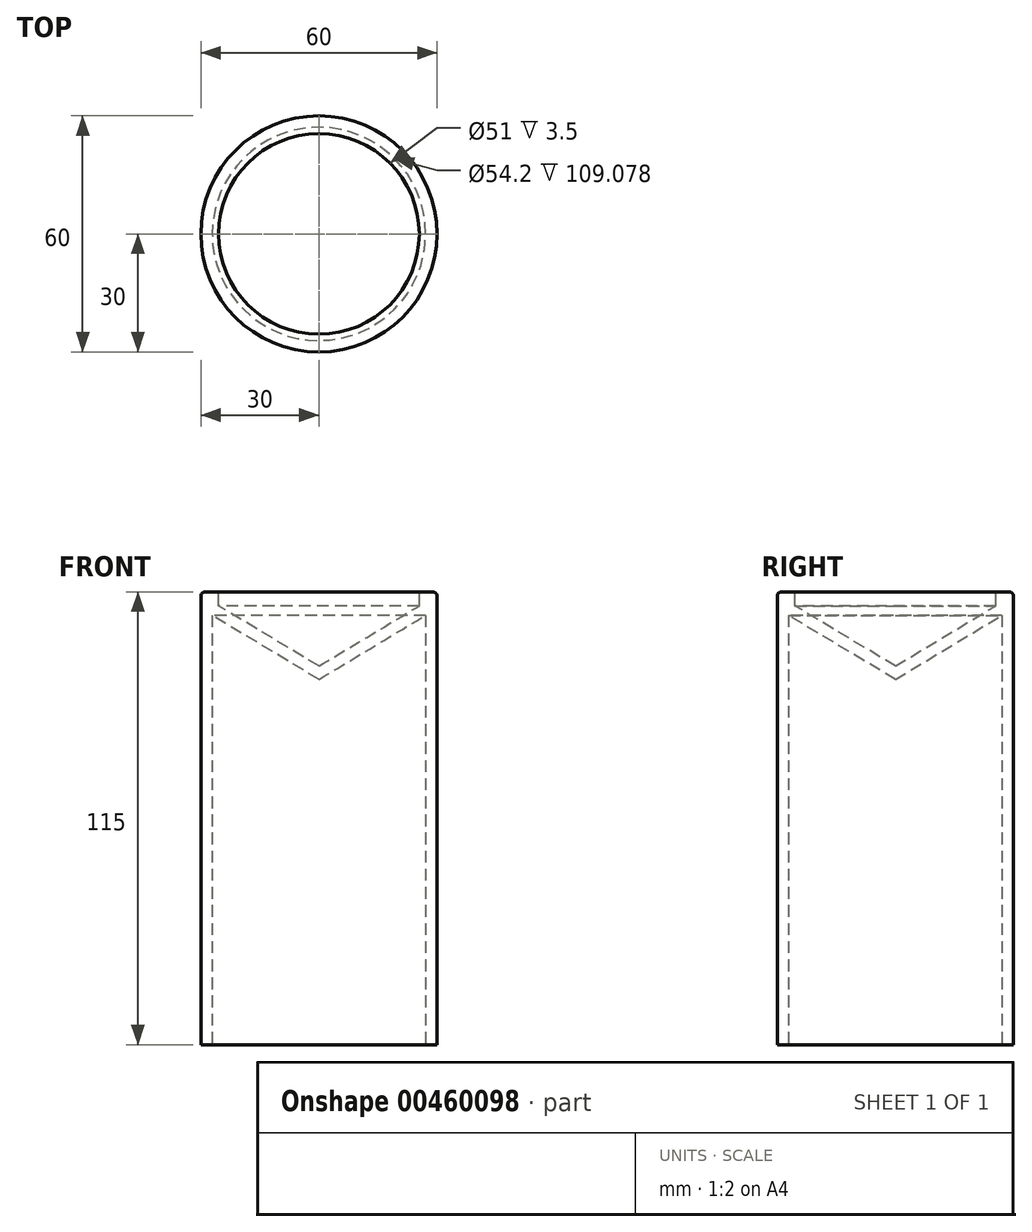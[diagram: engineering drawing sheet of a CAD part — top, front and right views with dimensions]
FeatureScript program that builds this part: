
annotation { "Feature Type Name" : "Feature", "Feature Type Description" : "" }
export const myFeature = defineFeature(function(context is Context, id is Id, definition is map)
    precondition{}
    {
        {
            var Q0;
            Q0=qCreatedBy(makeId("Top.planeOp"),FACE);
            var sketch = newSketch(context, id + "F0", { "sketchPlane" : qUnion([Q0])});
            skCircle(sketch, "E0", {"center": v(0, 0) * mm, "radius": 30 * mm});
            skSolve(sketch);
        }
        {
            var Q0;
            Q0=makeQuery(id+"F0.imprint","IMPRINT",FACE,{"disambiguationData":[TD([[makeQuery(id+"F0.imprint","IMPRINT",EDGE,{"derivedFrom":sQuery(id+"F0.wireOp",EDGE,"E0")}),1.0]])]});
            extrude(context, id + "F1", {"entities" : qUnion([Q0]), "depth" : 115 * mm});
        }
        {
            var Q0;
            Q0=qCreatedBy(makeId("Top.planeOp"),FACE);
            cPlane(context, id + "F2", {"entities" : qUnion([Q0]), "cplaneType" : CPlaneType.OFFSET, "offset" : 115 * mm, "width" : 150 * mm, "height" : 150 * mm});
        }
        {
            var Q0;
            Q0=qCreatedBy(id+"F2.planeOp",FACE);
            var sketch = newSketch(context, id + "F3", { "sketchPlane" : qUnion([Q0])});
            skCircle(sketch, "E1", {"center": v(0, 0) * mm, "radius": 30 * mm});
            skSolve(sketch);
        }
        {
            var Q0;
            Q0=sQuery(id+"F3.wireOp",VERTEX,"E1.center");
            var Q1;
            Q1=makeQuery(id+"F1.opExtrude","SWEPT_BODY",BODY,{"disambiguationData":[OSD([sQuery(id+"F0.wireOp",EDGE,"E0")])]});
            hole(context, id + "F4", {"style" : HoleStyle.SIMPLE, "endStyle" : HoleEndStyle.BLIND, "holeDiameter" : 51 * mm, "holeDepth" : 3.5 * mm, "isTappedThrough" : true, "tappedDepth" : 12 * mm, "tapClearance" : 3, "startFromSketch" : true, "locations" : qUnion([Q0]), "scope" : qUnion([Q1])});
        }
        {
            var Q0;
            Q0=makeQuery(id+"F1.opExtrude","CAP_EDGE",EDGE,{"disambiguationData":[OSD([sQuery(id+"F0.wireOp",EDGE,"E0")])],"isStart":false});
            var Q1;
            Q1=makeQuery(id+"F4.hole-0.boolean.opBoolean","COPY",EDGE,{"derivedFrom":makeQuery(id+"F4.hole-0.opRevolve","SWEPT_EDGE",EDGE,{"disambiguationData":[OSD([sQuery(id+"F4.hole-0.sketch.wireOp",EDGE,"core_line_2"),sQuery(id+"F4.hole-0.sketch.wireOp",EDGE,"core_line_3")])]})});
            fillet(context, id + "F5", {"entities" : qUnion([Q0, Q1]), "radius" : 1 * mm, "tangentPropagation" : true, "allowEdgeOverflow" : false});
        }
        {
            var Q0;
            Q0=makeQuery(id+"F1.opExtrude","CAP_FACE",FACE,{"disambiguationData":[OSD([sQuery(id+"F0.wireOp",EDGE,"E0")])],"isStart":true});
            shell(context, id + "F6", {"entities" : qUnion([Q0]), "thickness" : 2.9 * mm});
        }
    });
